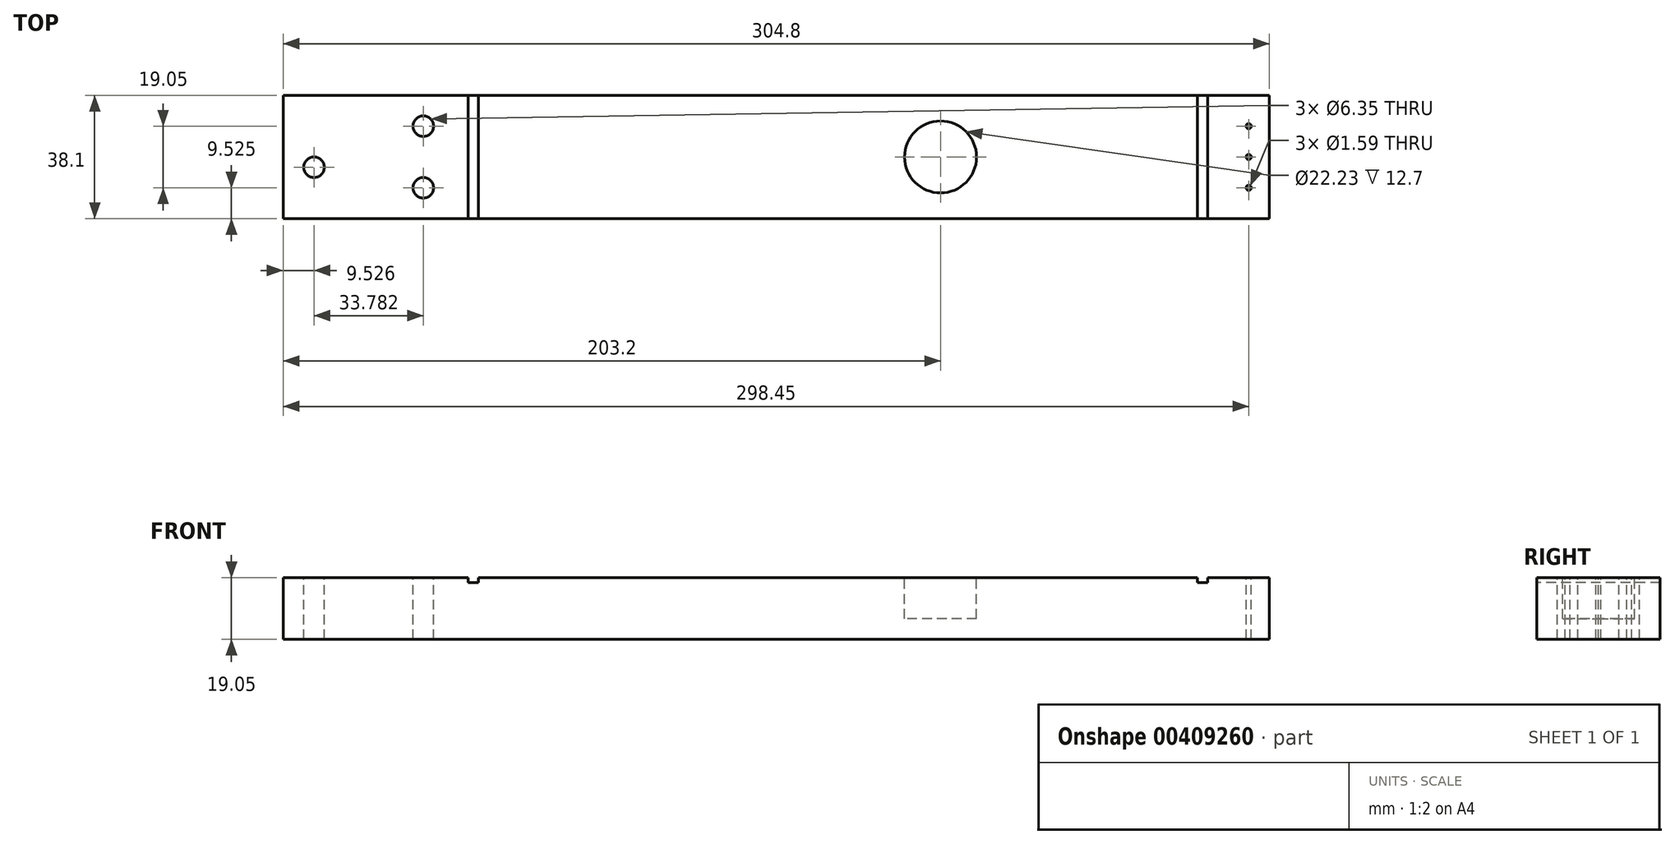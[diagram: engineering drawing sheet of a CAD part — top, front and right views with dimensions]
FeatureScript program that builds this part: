
annotation { "Feature Type Name" : "Feature", "Feature Type Description" : "" }
export const myFeature = defineFeature(function(context is Context, id is Id, definition is map)
    precondition{}
    {
        {
            var Q0;
            Q0=qCreatedBy(makeId("Top.planeOp"),FACE);
            var sketch = newSketch(context, id + "F0", { "sketchPlane" : qUnion([Q0])});
            skLineSegment(sketch, "E0.bottom", {"start": v(-67.92, 19.05) * mm, "end": v(236.88, 19.05) * mm});
            skLineSegment(sketch, "E0.top", {"start": v(-67.92, -19.05) * mm, "end": v(236.88, -19.05) * mm});
            skLineSegment(sketch, "E0.left", {"start": v(-67.92, 19.05) * mm, "end": v(-67.92, -19.05) * mm});
            skLineSegment(sketch, "E0.right", {"start": v(236.88, 19.05) * mm, "end": v(236.88, -19.05) * mm});
            skSolve(sketch);
        }
        {
            var Q0;
            Q0=qSketchRegion(id+"F0",true);
            extrude(context, id + "F1", {"entities" : qUnion([Q0]), "depth" : 19.05 * mm});
        }
        {
            var Q0;
            Q0=makeQuery(id+"F1.opExtrude","CAP_FACE",FACE,{"disambiguationData":[OSD([sQuery(id+"F0.wireOp",EDGE,"E0.bottom"),sQuery(id+"F0.wireOp",EDGE,"E0.top"),sQuery(id+"F0.wireOp",EDGE,"E0.left"),sQuery(id+"F0.wireOp",EDGE,"E0.right")])],"isStart":false});
            var sketch = newSketch(context, id + "F2", { "sketchPlane" : qUnion([Q0])});
            skCircle(sketch, "E1", {"center": v(135.28, 0) * mm, "radius": 11.11 * mm});
            skSolve(sketch);
        }
        {
            var Q0;
            Q0=qSketchRegion(id+"F2",true);
            extrude(context, id + "F3", {"entities" : qUnion([Q0]), "operationType" : NewBodyOperationType.REMOVE, "oppositeDirection" : true, "depth" : 12.7 * mm});
        }
        {
            var Q0;
            Q0=makeQuery(id+"F1.opExtrude","CAP_FACE",FACE,{"disambiguationData":[OSD([sQuery(id+"F0.wireOp",EDGE,"E0.bottom"),sQuery(id+"F0.wireOp",EDGE,"E0.top"),sQuery(id+"F0.wireOp",EDGE,"E0.left"),sQuery(id+"F0.wireOp",EDGE,"E0.right")])],"isStart":false});
            var sketch = newSketch(context, id + "F4", { "sketchPlane" : qUnion([Q0])});
            skCircle(sketch, "E2", {"center": v(-58.4, -3.18) * mm, "radius": 3.18 * mm});
            skPoint(sketch, "E3", {"position": v(-58.4, 0) * mm});
            skLineSegment(sketch, "E4", {"start": v(-58.4, 0) * mm, "end": v(135.28, 0) * mm, "construction": true});
            skSolve(sketch);
        }
        {
            var Q0;
            Q0=qSketchRegion(id+"F4",true);
            extrude(context, id + "F5", {"entities" : qUnion([Q0]), "operationType" : NewBodyOperationType.REMOVE, "endBound" : BoundingType.THROUGH_ALL, "oppositeDirection" : true, "depth" : 25.4 * mm});
        }
        {
            var Q0;
            Q0=makeQuery(id+"F1.opExtrude","CAP_FACE",FACE,{"disambiguationData":[OSD([sQuery(id+"F0.wireOp",EDGE,"E0.bottom"),sQuery(id+"F0.wireOp",EDGE,"E0.top"),sQuery(id+"F0.wireOp",EDGE,"E0.left"),sQuery(id+"F0.wireOp",EDGE,"E0.right")])],"isStart":false});
            var sketch = newSketch(context, id + "F6", { "sketchPlane" : qUnion([Q0])});
            skCircle(sketch, "E5", {"center": v(-24.61, -9.52) * mm, "radius": 3.18 * mm});
            skCircle(sketch, "E6", {"center": v(-24.61, 9.52) * mm, "radius": 3.18 * mm});
            skLineSegment(sketch, "E7", {"start": v(-61.89, 0) * mm, "end": v(-52.24, 0) * mm, "construction": true});
            skLineSegment(sketch, "E8", {"start": v(-28.72, 9.53) * mm, "end": v(-21.71, 9.53) * mm, "construction": true});
            skLineSegment(sketch, "E9", {"start": v(-29.2, -9.53) * mm, "end": v(-21.18, -9.53) * mm, "construction": true});
            skSolve(sketch);
        }
        {
            var Q0;
            Q0=qSketchRegion(id+"F6",true);
            extrude(context, id + "F7", {"entities" : qUnion([Q0]), "operationType" : NewBodyOperationType.REMOVE, "endBound" : BoundingType.THROUGH_ALL, "oppositeDirection" : true, "depth" : 25.4 * mm});
        }
        {
            var Q0;
            Q0=makeQuery(id+"F1.opExtrude","CAP_FACE",FACE,{"disambiguationData":[OSD([sQuery(id+"F0.wireOp",EDGE,"E0.bottom"),sQuery(id+"F0.wireOp",EDGE,"E0.top"),sQuery(id+"F0.wireOp",EDGE,"E0.left"),sQuery(id+"F0.wireOp",EDGE,"E0.right")])],"isStart":false});
            var sketch = newSketch(context, id + "F8", { "sketchPlane" : qUnion([Q0])});
            skLineSegment(sketch, "E10", {"start": v(230.53, 9.52) * mm, "end": v(230.53, -9.52) * mm, "construction": true});
            skCircle(sketch, "E11", {"center": v(230.53, 9.52) * mm, "radius": 0.8 * mm});
            skCircle(sketch, "E12", {"center": v(230.53, 0) * mm, "radius": 0.8 * mm});
            skCircle(sketch, "E13", {"center": v(230.53, -9.52) * mm, "radius": 0.8 * mm});
            skLineSegment(sketch, "E14", {"start": v(230.53, 0) * mm, "end": v(135.28, 0) * mm, "construction": true});
            skSolve(sketch);
        }
        {
            var Q0;
            Q0=qSketchRegion(id+"F8",true);
            extrude(context, id + "F9", {"entities" : qUnion([Q0]), "operationType" : NewBodyOperationType.REMOVE, "endBound" : BoundingType.THROUGH_ALL, "oppositeDirection" : true, "depth" : 25.4 * mm});
        }
        {
            var Q0;
            Q0=makeQuery(id+"F1.opExtrude","SWEPT_FACE",FACE,{"disambiguationData":[OSD([sQuery(id+"F0.wireOp",EDGE,"E0.top")])]});
            var sketch = newSketch(context, id + "F10", { "sketchPlane" : qUnion([Q0])});
            skLineSegment(sketch, "E15.bottom", {"start": v(-10.77, 19.05) * mm, "end": v(-7.6, 19.05) * mm});
            skLineSegment(sketch, "E15.top", {"start": v(-10.77, 17.46) * mm, "end": v(-7.6, 17.46) * mm});
            skLineSegment(sketch, "E15.left", {"start": v(-10.77, 19.05) * mm, "end": v(-10.77, 17.46) * mm});
            skLineSegment(sketch, "E15.right", {"start": v(-7.6, 19.05) * mm, "end": v(-7.6, 17.46) * mm});
            skLineSegment(sketch, "E16.bottom", {"start": v(214.66, 19.05) * mm, "end": v(217.83, 19.05) * mm});
            skLineSegment(sketch, "E16.top", {"start": v(214.66, 17.46) * mm, "end": v(217.83, 17.46) * mm});
            skLineSegment(sketch, "E16.left", {"start": v(214.66, 19.05) * mm, "end": v(214.66, 17.46) * mm});
            skLineSegment(sketch, "E16.right", {"start": v(217.83, 19.05) * mm, "end": v(217.83, 17.46) * mm});
            skSolve(sketch);
        }
        {
            var Q0;
            Q0=qSketchRegion(id+"F10",true);
            extrude(context, id + "F11", {"entities" : qUnion([Q0]), "operationType" : NewBodyOperationType.REMOVE, "endBound" : BoundingType.THROUGH_ALL, "oppositeDirection" : true, "depth" : 25.4 * mm});
        }
    });
